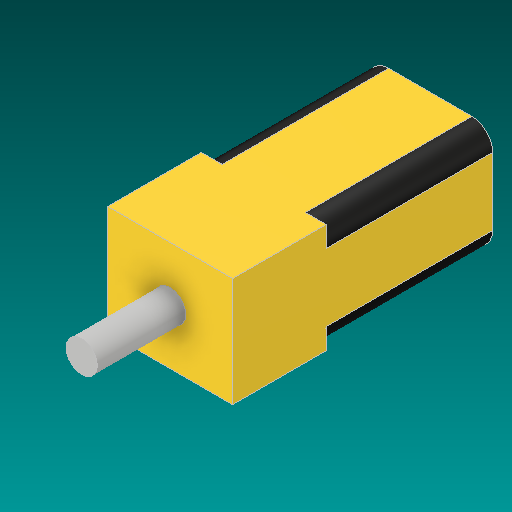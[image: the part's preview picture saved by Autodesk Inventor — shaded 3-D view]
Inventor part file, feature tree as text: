
AUTODESK INVENTOR PART (.ipt)
format: ipt  version: 2020 (Build 240168000, 168)  size: 142,336 bytes
history: native  units: mm
features: extrude x3, sketch x3, fillet x1
ambient origin geometry x8: Origin, YZ Plane, XZ Plane, XY Plane, X Axis, Y Axis, Z Axis, Center Point
bodies: Solid1 (feature_tree)
feature tree (7):
  extrude  "Extrusion1"  Depth=10.5mm
  fillet  "Fillet1"  Radius=16.0mm
  extrude  "Extrusion2"  Depth=9.0mm TaperAngle=0.0deg
  extrude  "Extrusion3"  Depth=8.5mm TaperAngle=0.0deg
  sketch  "Sketch1"  dims[d0=12.0mm d2=10.5mm d3=16.0mm d4=0.0mm]
  sketch  "Sketch2"  dims[d5=2.0mm d6=9.0mm d7=0.0mm]
  sketch  "Sketch3"  dims[d8=3.0mm d9=8.5mm d10=0.0mm]
